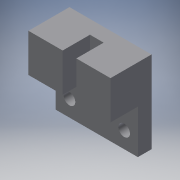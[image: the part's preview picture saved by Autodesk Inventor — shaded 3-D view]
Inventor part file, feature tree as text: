
AUTODESK INVENTOR PART (.ipt)
format: ipt  version: 2019 (Build 230136000, 136)  size: 116,224 bytes
history: native  units: in
note: dims shown in document units (in); Inventor stores cm internally (conversion verified against a paired STEP export)
features: extrude x2, sketch x2
ambient origin geometry x8: Origin, YZ Plane, XZ Plane, XY Plane, X Axis, Y Axis, Z Axis, Center Point
bodies: Solid1 (feature_tree)
feature tree (4):
  extrude  "Extrusion1"  Depth=1.1811in
  extrude  "Extrusion2"  Depth=0.1969in
  sketch  "Sketch1"  dims[d2=1.1811in d3=1.1811in]
  sketch  "Sketch2"  dims[d4=0.1969in d5=0.0in d6=0.1969in d7=0.5512in d8=0.3937in d9=0.0in d10=0.1673in d11=0.1673in d12=0.1969in d13=0.2362in]
